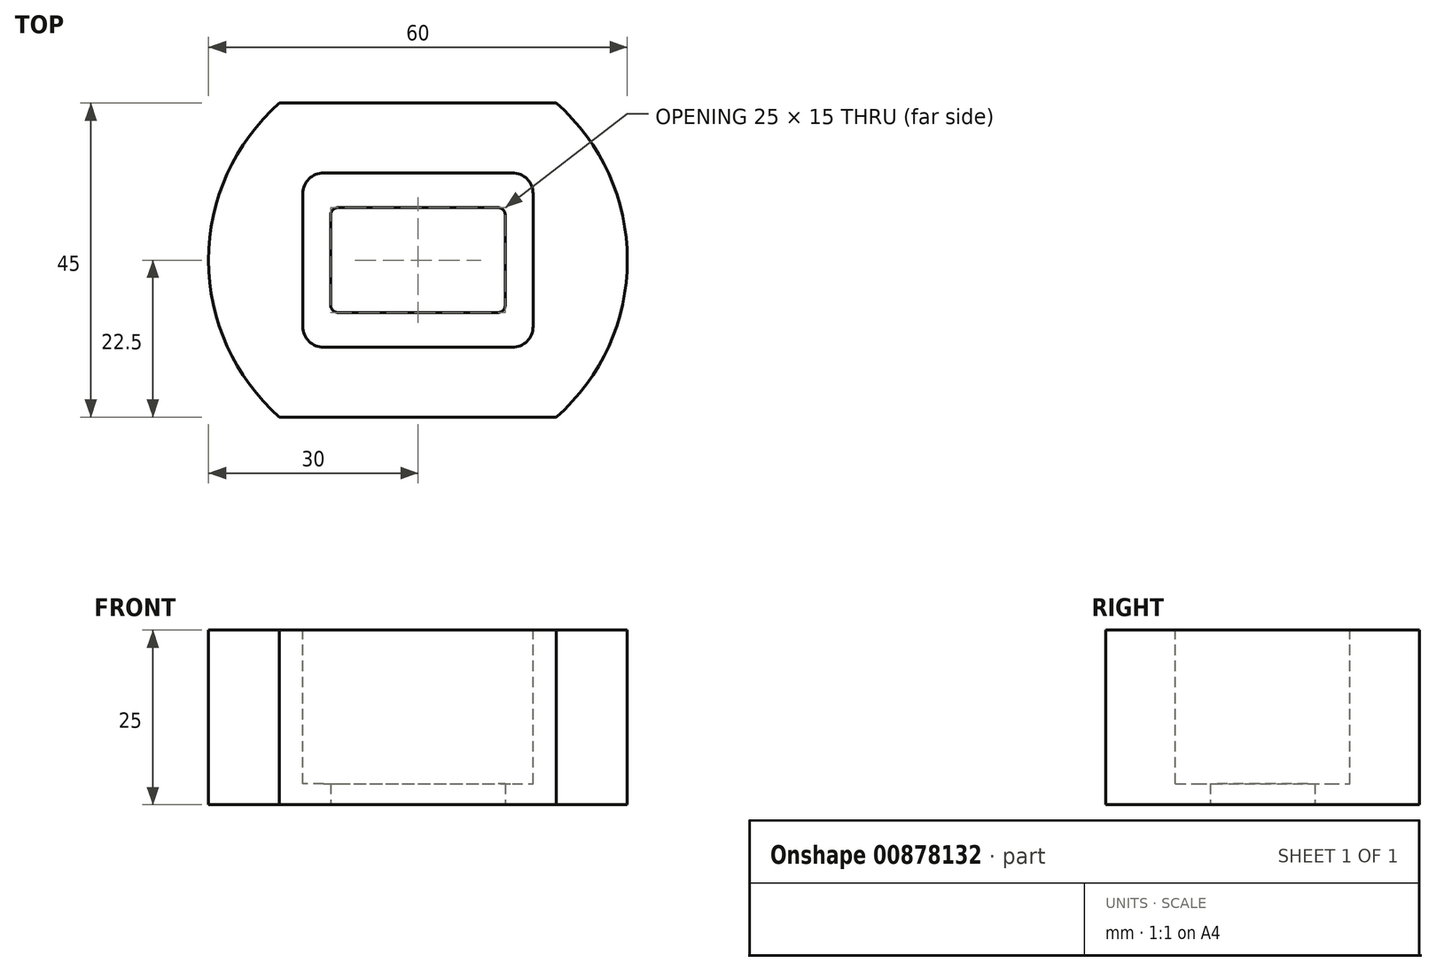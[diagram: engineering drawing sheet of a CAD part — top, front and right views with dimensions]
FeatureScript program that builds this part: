
annotation { "Feature Type Name" : "Feature", "Feature Type Description" : "" }
export const myFeature = defineFeature(function(context is Context, id is Id, definition is map)
    precondition{}
    {
        {
            var Q0;
            Q0=qCreatedBy(makeId("Top.planeOp"),FACE);
            var sketch = newSketch(context, id + "F0", { "sketchPlane" : qUnion([Q0])});
            skArc(sketch, "E0", {"start": v(-19.84, 22.5) * mm, "mid": v(-30, 0) * mm, "end": v(-19.84, -22.5) * mm});
            skLineSegment(sketch, "E1.bottom", {"start": v(-19.84, -22.5) * mm, "end": v(19.84, -22.5) * mm});
            skLineSegment(sketch, "E1.top", {"start": v(-19.84, 22.5) * mm, "end": v(19.84, 22.5) * mm});
            skArc(sketch, "E2.trimOffspring", {"start": v(19.84, -22.5) * mm, "mid": v(30, 0) * mm, "end": v(19.84, 22.5) * mm});
            skSolve(sketch);
        }
        {
            var Q0;
            Q0=makeQuery(id+"F0.imprint","IMPRINT",FACE,{"disambiguationData":[TD([[makeQuery(id+"F0.imprint","IMPRINT",EDGE,{"derivedFrom":sQuery(id+"F0.wireOp",EDGE,"E0")}),1.0]])]});
            var sketch = newSketch(context, id + "F1", { "sketchPlane" : qUnion([Q0])});
            skLineSegment(sketch, "E3", {"start": v(-53.07, 0) * mm, "end": v(16.5, 0) * mm, "construction": true});
            skLineSegment(sketch, "E4", {"start": v(0, 12.5) * mm, "end": v(0, -37.98) * mm, "construction": true});
            skLineSegment(sketch, "E5.bottom", {"start": v(-13.5, -12.5) * mm, "end": v(13.5, -12.5) * mm});
            skLineSegment(sketch, "E5.top", {"start": v(-13.5, 12.5) * mm, "end": v(13.5, 12.5) * mm});
            skLineSegment(sketch, "E5.left", {"start": v(-16.5, -9.5) * mm, "end": v(-16.5, 9.5) * mm});
            skLineSegment(sketch, "E5.right", {"start": v(16.5, -9.5) * mm, "end": v(16.5, 9.5) * mm});
            skPoint(sketch, "E6.visualSharp", {"position": v(16.5, 12.5) * mm});
            skArc(sketch, "E6.filletArc", {"start": v(16.5, 9.5) * mm, "mid": v(15.62, 11.62) * mm, "end": v(13.5, 12.5) * mm});
            skPoint(sketch, "E7.visualSharp", {"position": v(16.5, -12.5) * mm});
            skArc(sketch, "E7.filletArc", {"start": v(13.5, -12.5) * mm, "mid": v(15.62, -11.62) * mm, "end": v(16.5, -9.5) * mm});
            skPoint(sketch, "E8.visualSharp", {"position": v(-16.5, -12.5) * mm});
            skArc(sketch, "E8.filletArc", {"start": v(-16.5, -9.5) * mm, "mid": v(-15.62, -11.62) * mm, "end": v(-13.5, -12.5) * mm});
            skPoint(sketch, "E9.visualSharp", {"position": v(-16.5, 12.5) * mm});
            skArc(sketch, "E9.filletArc", {"start": v(-13.5, 12.5) * mm, "mid": v(-15.62, 11.62) * mm, "end": v(-16.5, 9.5) * mm});
            skSolve(sketch);
        }
        {
            var Q0;
            Q0 = qSketchRegion(id + "F0", true);
            extrude(context, id + "F2", {"entities" : qUnion([Q0]), "oppositeDirection" : true, "depth" : 25 * mm, "offsetDistance" : 25 * mm});
        }
        {
            var Q0;
            Q0 = qSketchRegion(id + "F1", true);
            extrude(context, id + "F3", {"entities" : qUnion([Q0]), "operationType" : NewBodyOperationType.REMOVE, "oppositeDirection" : true, "depth" : 22 * mm, "offsetDistance" : 25 * mm});
        }
        {
            var Q0;
            Q0=makeQuery(id+"F2.opExtrude","CAP_FACE",FACE,{"disambiguationData":[OSD([sQuery(id+"F0.wireOp",EDGE,"E0"),sQuery(id+"F0.wireOp",EDGE,"E1.bottom"),sQuery(id+"F0.wireOp",EDGE,"E1.top"),sQuery(id+"F0.wireOp",EDGE,"E2.trimOffspring")])],"isStart":false});
            var sketch = newSketch(context, id + "F4", { "sketchPlane" : qUnion([Q0])});
            skLineSegment(sketch, "E10", {"start": v(-39.66, 0) * mm, "end": v(12.5, 0) * mm, "construction": true});
            skLineSegment(sketch, "E11", {"start": v(0, 7.5) * mm, "end": v(0, -50.58) * mm, "construction": true});
            skLineSegment(sketch, "E12.bottom", {"start": v(-11.5, -7.5) * mm, "end": v(11.5, -7.5) * mm});
            skLineSegment(sketch, "E12.top", {"start": v(-11.5, 7.5) * mm, "end": v(11.5, 7.5) * mm});
            skLineSegment(sketch, "E12.left", {"start": v(-12.5, -6.5) * mm, "end": v(-12.5, 6.5) * mm});
            skLineSegment(sketch, "E12.right", {"start": v(12.5, -6.5) * mm, "end": v(12.5, 6.5) * mm});
            skPoint(sketch, "E13.visualSharp", {"position": v(12.5, -7.5) * mm});
            skArc(sketch, "E13.filletArc", {"start": v(11.5, -7.5) * mm, "mid": v(12.2, -7.2) * mm, "end": v(12.5, -6.5) * mm});
            skPoint(sketch, "E14.visualSharp", {"position": v(12.5, 7.5) * mm});
            skArc(sketch, "E14.filletArc", {"start": v(12.5, 6.5) * mm, "mid": v(12.2, 7.2) * mm, "end": v(11.5, 7.5) * mm});
            skPoint(sketch, "E15.visualSharp", {"position": v(-12.5, 7.5) * mm});
            skArc(sketch, "E15.filletArc", {"start": v(-11.5, 7.5) * mm, "mid": v(-12.2, 7.2) * mm, "end": v(-12.5, 6.5) * mm});
            skPoint(sketch, "E16.visualSharp", {"position": v(-12.5, -7.5) * mm});
            skArc(sketch, "E16.filletArc", {"start": v(-12.5, -6.5) * mm, "mid": v(-12.2, -7.2) * mm, "end": v(-11.5, -7.5) * mm});
            skSolve(sketch);
        }
        {
            var Q0;
            Q0 = qSketchRegion(id + "F4", true);
            extrude(context, id + "F5", {"entities" : qUnion([Q0]), "operationType" : NewBodyOperationType.REMOVE, "endBound" : BoundingType.UP_TO_NEXT, "oppositeDirection" : true, "depth" : 25 * mm, "offsetDistance" : 25 * mm});
        }
    });
